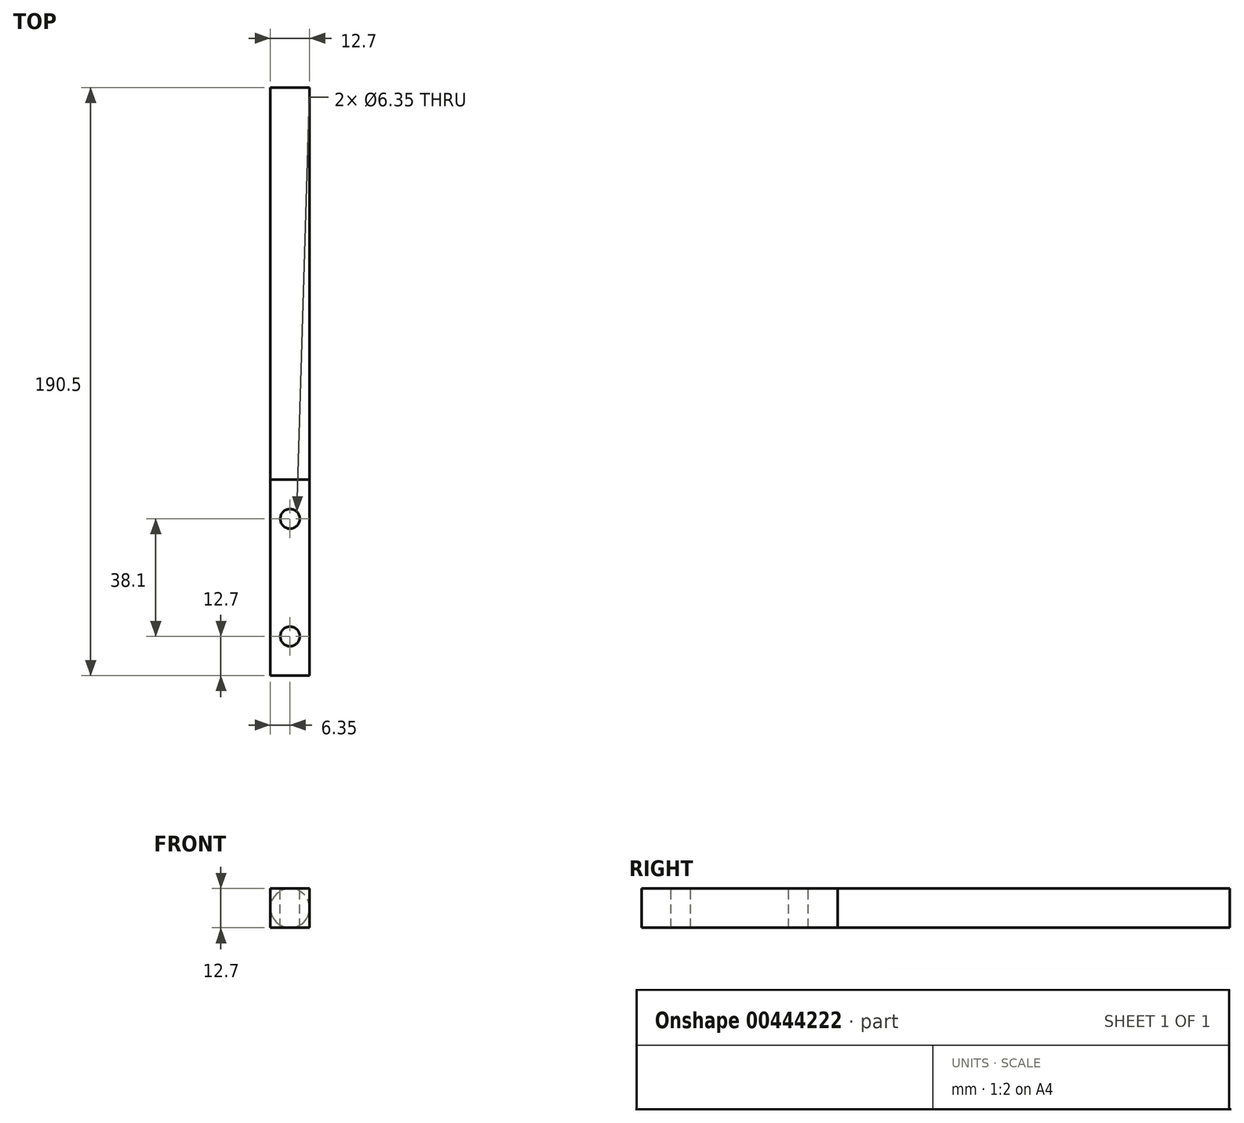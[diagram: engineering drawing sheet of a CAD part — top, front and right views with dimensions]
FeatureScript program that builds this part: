
annotation { "Feature Type Name" : "Feature", "Feature Type Description" : "" }
export const myFeature = defineFeature(function(context is Context, id is Id, definition is map)
    precondition{}
    {
        {
            var Q0;
            Q0=qCreatedBy(makeId("Front.planeOp"),FACE);
            var sketch = newSketch(context, id + "F0", { "sketchPlane" : qUnion([Q0])});
            skLineSegment(sketch, "E0.bottom", {"start": v(-6.35, 6.35) * mm, "end": v(6.35, 6.35) * mm});
            skLineSegment(sketch, "E0.top", {"start": v(-6.35, -6.35) * mm, "end": v(6.35, -6.35) * mm});
            skLineSegment(sketch, "E0.left", {"start": v(-6.35, 6.35) * mm, "end": v(-6.35, -6.35) * mm});
            skLineSegment(sketch, "E0.right", {"start": v(6.35, 6.35) * mm, "end": v(6.35, -6.35) * mm});
            skSolve(sketch);
        }
        {
            var Q0;
            Q0 = qSketchRegion(id + "F0", true);
            extrude(context, id + "F1", {"entities" : qUnion([Q0]), "depth" : 12.7 * mm, "hasSecondDirection" : true, "secondDirectionOppositeDirection" : true, "secondDirectionDepth" : 177.8 * mm});
        }
        {
            var Q0;
            Q0=makeQuery(id+"F1.opExtrude","CAP_FACE",FACE,{"disambiguationData":[OSD([sQuery(id+"F0.wireOp",EDGE,"E0.bottom"),sQuery(id+"F0.wireOp",EDGE,"E0.top"),sQuery(id+"F0.wireOp",EDGE,"E0.left"),sQuery(id+"F0.wireOp",EDGE,"E0.right")])],"isStart":true});
            var sketch = newSketch(context, id + "F2", { "sketchPlane" : qUnion([Q0])});
            skCircle(sketch, "E1", {"center": v(0, 0) * mm, "radius": 6.35 * mm});
            skPoint(sketch, "E2.0", {"position": v(-6.35, 6.35) * mm});
            skLineSegment(sketch, "E3.bottom", {"start": v(-6.35, 6.35) * mm, "end": v(6.35, 6.35) * mm});
            skLineSegment(sketch, "E3.top", {"start": v(-6.35, -6.35) * mm, "end": v(6.35, -6.35) * mm});
            skLineSegment(sketch, "E3.left", {"start": v(-6.35, 6.35) * mm, "end": v(-6.35, -6.35) * mm});
            skLineSegment(sketch, "E3.right", {"start": v(6.35, 6.35) * mm, "end": v(6.35, -6.35) * mm});
            skSolve(sketch);
        }
        {
            var Q0;
            Q0 = qSketchRegion(id + "F2", true);
            extrude(context, id + "F3", {"entities" : qUnion([Q0]), "operationType" : NewBodyOperationType.REMOVE, "oppositeDirection" : true, "depth" : 127 * mm});
        }
        {
            var Q0;
            Q0=makeQuery(id+"F3.boolean.opBoolean","COPY",FACE,{"derivedFrom":makeQuery(id+"F3.opExtrude","CAP_FACE",FACE,{"disambiguationData":[OSD([sQuery(id+"F2.wireOp",EDGE,"E3.bottom"),sQuery(id+"F2.wireOp",EDGE,"E3.top"),sQuery(id+"F2.wireOp",EDGE,"E3.left"),sQuery(id+"F2.wireOp",EDGE,"E3.right")])],"isStart":false})});
            var sketch = newSketch(context, id + "F4", { "sketchPlane" : qUnion([Q0])});
            skCircle(sketch, "E4", {"center": v(0, 0) * mm, "radius": 6.35 * mm});
            skSolve(sketch);
        }
        {
            var Q0;
            Q0 = qSketchRegion(id + "F4", true);
            extrude(context, id + "F5", {"entities" : qUnion([Q0]), "operationType" : NewBodyOperationType.ADD, "depth" : 127 * mm});
        }
        {
            var Q0;
            Q0=makeQuery(id+"F1.opExtrude","SWEPT_FACE",FACE,{"disambiguationData":[OSD([sQuery(id+"F0.wireOp",EDGE,"E0.bottom")])]});
            var sketch = newSketch(context, id + "F6", { "sketchPlane" : qUnion([Q0])});
            skCircle(sketch, "E5", {"center": v(0, 38.1) * mm, "radius": 3.18 * mm});
            skCircle(sketch, "E6", {"center": v(0, 0) * mm, "radius": 3.18 * mm});
            skSolve(sketch);
        }
        {
            var Q0;
            Q0 = qSketchRegion(id + "F6", true);
            extrude(context, id + "F7", {"entities" : qUnion([Q0]), "operationType" : NewBodyOperationType.REMOVE, "oppositeDirection" : true, "depth" : 25.4 * mm});
        }
    });
